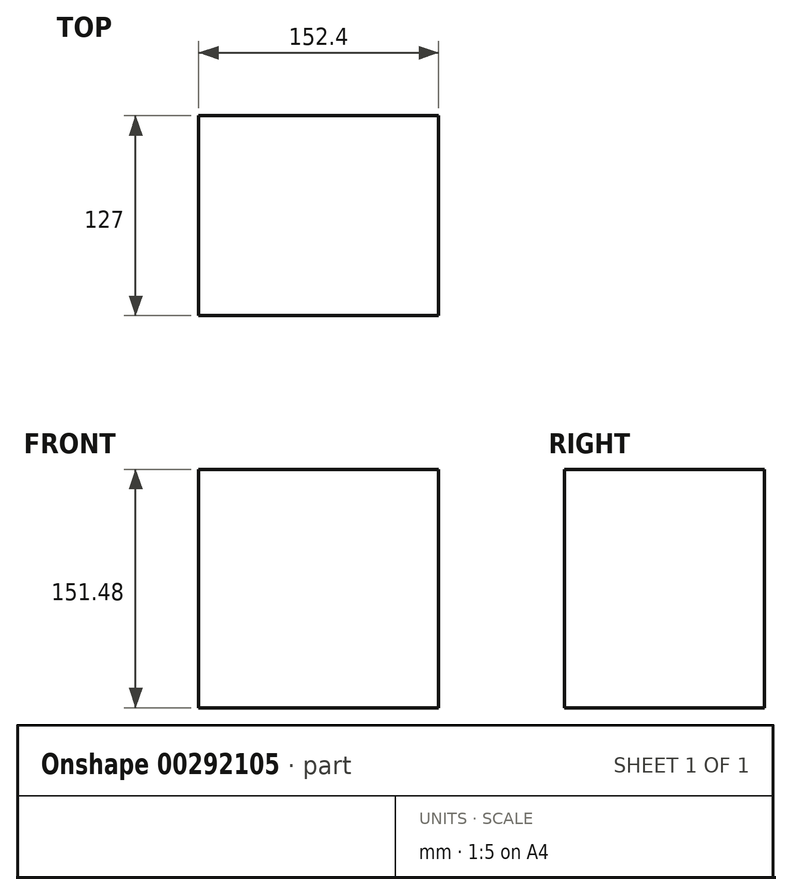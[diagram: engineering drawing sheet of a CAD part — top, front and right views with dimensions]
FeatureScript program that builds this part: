
annotation { "Feature Type Name" : "Feature", "Feature Type Description" : "" }
export const myFeature = defineFeature(function(context is Context, id is Id, definition is map)
    precondition{}
    {
        {
            var Q0;
            Q0=qCreatedBy(makeId("Front.planeOp"),FACE);
            var sketch = newSketch(context, id + "F0", { "sketchPlane" : qUnion([Q0])});
            skLineSegment(sketch, "E0.bottom", {"start": v(-76.2, -75.74) * mm, "end": v(76.2, -75.74) * mm});
            skLineSegment(sketch, "E0.top", {"start": v(-76.2, 75.74) * mm, "end": v(76.2, 75.74) * mm});
            skLineSegment(sketch, "E0.left", {"start": v(-76.2, -75.74) * mm, "end": v(-76.2, 75.74) * mm});
            skLineSegment(sketch, "E0.right", {"start": v(76.2, -75.74) * mm, "end": v(76.2, 75.74) * mm});
            skPoint(sketch, "E0.middle", {"position": v(0, 0) * mm});
            skSolve(sketch);
        }
        {
            var Q0;
            Q0 = qSketchRegion(id + "F0", true);
            extrude(context, id + "F1", {"entities" : qUnion([Q0]), "depth" : 127 * mm});
        }
    });
